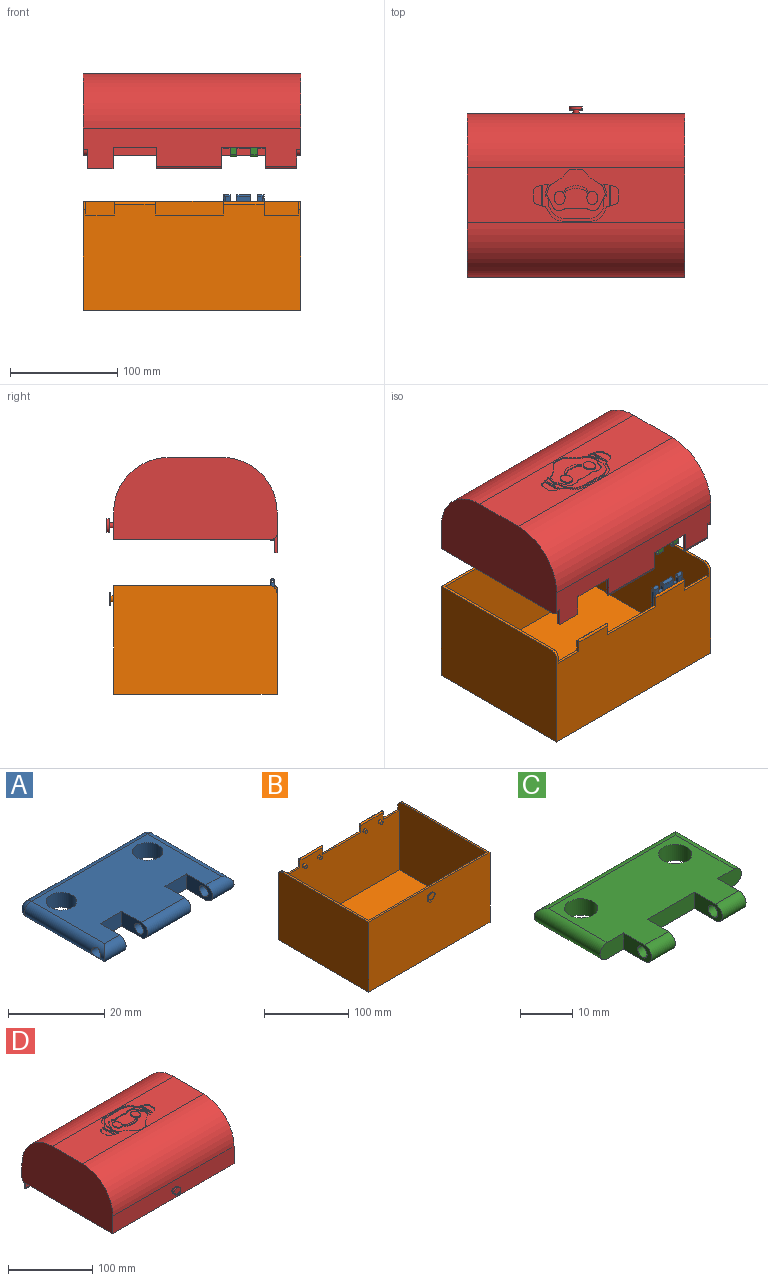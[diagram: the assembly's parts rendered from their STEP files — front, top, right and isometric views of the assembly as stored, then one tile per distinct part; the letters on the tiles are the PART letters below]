
ASSEMBLY  parts=4 mates=7
PART A: 21 faces, bbox 38.1x25.4x3.8 mm
  f0: plane 7.62x3.81mm, normal (-1,0,0), area 22.4mm2, adj f7,f8,f9,f12,f16
  f1: plane 7.62x3.81mm, normal (1,0,0), area 22.4mm2, adj f2,f8,f9,f11,f14
  f2: plane 6.35x3.81mm, normal (0,-1,0), area 24.2mm2, adj f1,f3,f8,f9
  f3: plane 7.62x3.81mm, normal (-1,0,0), area 22.4mm2, adj f2,f8,f9,f10,f13
  f4: plane 7.62x3.81mm, normal (1,0,0), area 22.4mm2, adj f7,f8,f9,f10,f13
  f5: cylinder r=3.17mm len=6.35mm, axis (0,0,-1), area 76mm2, adj f8,f9
  f6: cylinder r=3.17mm len=6.35mm, axis (0,0,-1), area 76mm2, adj f8,f9
  f7: plane 6.35x3.81mm, normal (0,-1,0), area 24.2mm2, adj f0,f4,f8,f9
  f8: plane 34.29x21.59mm, normal (0,0,1), area 604.4mm2, adj f0,f1,f2,f3,f4,f5,f6,f7
  f9: plane 34.29x21.59mm, normal (0,0,-1), area 604.4mm2, adj f0,f1,f2,f3,f4,f5,f6,f7
  f10: cylinder r=1.27mm len=12.7mm, axis (-1,0,0), area 101.3mm2, adj f3,f4
  f11: cylinder r=1.27mm len=6.35mm, axis (-1,0,0), area 48.8mm2, adj f1,f15
  f12: cylinder r=1.27mm len=6.35mm, axis (-1,0,0), area 48.8mm2, adj f0,f18
  f13: cylinder r=1.91mm len=12.7mm, axis (-1,0,0), area 76mm2, adj f3,f4,f8,f9
  f14: cylinder r=1.91mm len=6.36mm, axis (-1,0,0), area 33.9mm2, adj f1,f8,f9,f15
  f15: cylinder r=1.91mm len=23.5mm, axis (0,1,0), area 131.1mm2, adj f8,f9,f11,f14,f17
  f16: cylinder r=1.91mm len=6.36mm, axis (-1,0,0), area 33.9mm2, adj f0,f8,f9,f18
  f17: sphere r=1.91mm, area 11.4mm2, adj f15,f19
  f18: cylinder r=1.91mm len=23.5mm, axis (0,-1,0), area 131.1mm2, adj f8,f9,f12,f16,f20
  f19: cylinder r=1.91mm len=34.29mm, axis (1,0,0), area 205.2mm2, adj f8,f9,f17,f20
  f20: sphere r=1.91mm, area 11.4mm2, adj f18,f19
PART B: 39 faces, bbox 203.2x156.2x101.6 mm
  f0: plane 203.2x144.78mm, normal (0,0,1), area 1238.7mm2, adj f3,f4,f5,f7,f8,f9,f30,f31
  f1: plane 203.2x99.06mm, normal (0,1,0), area 18864.5mm2, adj f3,f5,f6,f7,f9,f19,f20,f21
  f2: plane 198.12x96.52mm, normal (0,-1,0), area 17821.8mm2, adj f7,f9,f10,f11,f13,f15,f17,f19
  f3: plane 152.4x101.6mm, normal (-1,0,0), area 15471.4mm2, adj f0,f1,f4,f6,f31
  f4: plane 203.2x101.6mm, normal (0,-1,0), area 20613.5mm2, adj f0,f3,f5,f6,f32
  f5: plane 152.4x101.6mm, normal (1,0,0), area 15471.4mm2, adj f0,f1,f4,f6,f30
  f6: plane 203.2x152.4mm, normal (0,0,-1), area 30967.7mm2, adj f1,f3,f4,f5
  f7: plane 149.86x99.06mm, normal (1,0,0), area 14613.3mm2, adj f0,f1,f2,f8,f10,f25,f31
  f8: plane 198.12x99.06mm, normal (0,1,0), area 19625.8mm2, adj f0,f7,f9,f10
  f9: plane 149.86x99.06mm, normal (-1,0,0), area 14613.3mm2, adj f0,f1,f2,f8,f10,f23,f30
  f10: plane 198.12x147.32mm, normal (0,0,1), area 29187mm2, adj f2,f7,f8,f9
  f11: cylinder r=2.22mm len=4.45mm, axis (0,1,0), area 53.2mm2, adj f2,f12
  f12: plane 4.45x4.45mm, normal (0,-1,0), area 15.5mm2, adj f11
  f13: cylinder r=2.22mm len=4.45mm, axis (0,1,0), area 53.2mm2, adj f2,f14
  f14: plane 4.45x4.45mm, normal (0,-1,0), area 15.5mm2, adj f13
  f15: cylinder r=2.22mm len=4.45mm, axis (0,1,0), area 53.2mm2, adj f2,f16
  f16: plane 4.45x4.45mm, normal (0,-1,0), area 15.5mm2, adj f15
  f17: cylinder r=2.22mm len=4.45mm, axis (0,1,0), area 53.2mm2, adj f2,f18
  f18: plane 4.45x4.45mm, normal (0,-1,0), area 15.5mm2, adj f17
  f19: plane 12.36x2.54mm, normal (1,0,0), area 29.8mm2, adj f1,f2,f21,f28,f29
  f20: plane 12.36x2.54mm, normal (-1,0,0), area 29.8mm2, adj f1,f2,f21,f26,f27
  f21: plane 63.5x2.54mm, normal (0,0,1), area 161.3mm2, adj f1,f2,f19,f20
  f22: plane 12.36x2.54mm, normal (1,0,0), area 29.8mm2, adj f1,f2,f23,f26,f27
  f23: plane 26.67x2.54mm, normal (0,0,1), area 67.7mm2, adj f1,f2,f9,f22
  f24: plane 12.36x2.54mm, normal (-1,0,0), area 29.8mm2, adj f1,f2,f25,f28,f29
  f25: plane 31.75x2.54mm, normal (0,0,1), area 80.6mm2, adj f1,f2,f7,f24
  f26: cylinder r=2.54mm len=38.1mm, axis (-1,0,0), area 101.3mm2, adj f2,f20,f22,f27
  f27: cylinder r=2.54mm len=38.1mm, axis (1,0,0), area 101.3mm2, adj f1,f20,f22,f26
  f28: cylinder r=2.54mm len=38.1mm, axis (-1,0,0), area 101.3mm2, adj f2,f19,f24,f29
  f29: cylinder r=2.54mm len=38.1mm, axis (1,0,0), area 101.3mm2, adj f1,f19,f24,f28
  f30: cylinder r=7.62mm len=7.62mm, axis (1,0,0), area 30.4mm2, adj f0,f1,f5,f9
  f31: cylinder r=7.62mm len=7.62mm, axis (1,0,0), area 30.4mm2, adj f0,f1,f3,f7
  f32: cylinder r=3.17mm len=6.35mm, axis (0,1,0), area 60.1mm2, adj f4,f35,f36,f37,f38
  f33: cylinder r=6.35mm len=12.7mm, axis (0,1,0), area 32.8mm2, adj f34,f36,f37,f38
  f34: plane 6.27x5.02mm, normal (0.78,0,0.62), area 10.2mm2, adj f33,f35,f37,f38
  f35: cylinder r=3.17mm len=2.1mm, axis (0,1,0), area 3.1mm2, adj f32,f34,f37,f38
  f36: cylinder r=3.17mm len=5.06mm, axis (0,1,0), area 8.4mm2, adj f32,f33,f37,f38
  f37: plane 12.7x12.07mm, normal (0,-1,0), area 96.2mm2, adj f32,f33,f34,f35,f36
  f38: plane 12.7x12.07mm, normal (0,1,0), area 64.5mm2, adj f32,f33,f34,f35,f36
PART C: 18 faces, bbox 38.1x25.4x3.8 mm
  f0: plane 6.35x3.81mm, normal (0,-1,0), area 22.6mm2, adj f1,f9,f10,f15
  f1: plane 7.62x3.81mm, normal (-1,0,0), area 22.4mm2, adj f0,f9,f10,f12,f14
  f2: plane 7.62x3.81mm, normal (1,0,0), area 22.4mm2, adj f3,f9,f10,f12,f14
  f3: plane 12.7x3.81mm, normal (0,-1,0), area 48.4mm2, adj f2,f4,f9,f10
  f4: plane 7.62x3.81mm, normal (-1,0,0), area 22.4mm2, adj f3,f9,f10,f11,f13
  f5: plane 7.62x3.81mm, normal (1,0,0), area 22.4mm2, adj f6,f9,f10,f11,f13
  f6: plane 6.35x3.81mm, normal (0,-1,0), area 22.6mm2, adj f5,f9,f10,f16
  f7: cylinder r=3.17mm len=6.35mm, axis (0,0,-1), area 76mm2, adj f9,f10
  f8: cylinder r=3.17mm len=6.35mm, axis (0,0,-1), area 76mm2, adj f9,f10
  f9: plane 34.29x21.59mm, normal (0,0,1), area 553.6mm2, adj f0,f1,f2,f3,f4,f5,f6,f7
  f10: plane 34.29x21.59mm, normal (0,0,-1), area 553.6mm2, adj f0,f1,f2,f3,f4,f5,f6,f7
  f11: cylinder r=1.27mm len=6.35mm, axis (-1,0,0), area 50.7mm2, adj f4,f5
  f12: cylinder r=1.27mm len=6.35mm, axis (-1,0,0), area 50.7mm2, adj f1,f2
  f13: cylinder r=1.91mm len=6.35mm, axis (-1,0,0), area 38mm2, adj f4,f5,f9,f10
  f14: cylinder r=1.91mm len=6.35mm, axis (-1,0,0), area 38mm2, adj f1,f2,f9,f10
  f15: cylinder r=1.91mm len=17.79mm, axis (0,1,0), area 102.3mm2, adj f0,f9,f10,f17
  f16: cylinder r=1.91mm len=17.79mm, axis (0,-1,0), area 102.3mm2, adj f6,f9,f10,f17
  f17: cylinder r=1.91mm len=38.11mm, axis (1,0,0), area 219.7mm2, adj f9,f10,f15,f16
PART D: 136 faces, bbox 203.2x158.8x88.9 mm
  f0: plane 203.2x147.32mm, normal (0,0,-1), area 1251.6mm2, adj f2,f3,f4,f8,f9,f10,f94,f97
  f1: plane 203.2x50.8mm, normal (0,0,1), area 8219.7mm2, adj f2,f4,f6,f7,f22,f23,f24,f25
  f2: plane 152.4x76.2mm, normal (-1,0,0), area 10499.7mm2, adj f0,f1,f3,f5,f6,f7,f97
  f3: plane 203.2x25.4mm, normal (0,-1,0), area 5141mm2, adj f0,f2,f4,f6,f15
  f4: plane 152.4x76.2mm, normal (1,0,0), area 10499.7mm2, adj f0,f1,f3,f5,f6,f7,f94
  f5: plane 203.2x38.1mm, normal (0,1,0), area 5725.8mm2, adj f2,f4,f7,f81,f82,f83,f84,f85
  f6: cylinder r=50.8mm len=203.2mm, axis (-1,0,0), area 16214.6mm2, adj f1,f2,f3,f4
  f7: cylinder r=50.8mm len=203.2mm, axis (1,0,0), area 16214.6mm2, adj f1,f2,f4,f5
  f8: plane 147.32x73.66mm, normal (1,0,0), area 9851.4mm2, adj f0,f9,f11,f12,f13,f14,f97
  f9: plane 198.12x25.4mm, normal (0,1,0), area 5032.2mm2, adj f0,f8,f10,f13
  f10: plane 147.32x73.66mm, normal (-1,0,0), area 9851.4mm2, adj f0,f9,f11,f12,f13,f14,f94
  f11: plane 198.12x38.1mm, normal (0,-1,0), area 5552.7mm2, adj f8,f10,f14,f73,f75,f77,f79,f81
  f12: plane 198.12x50.8mm, normal (0,0,-1), area 10064.5mm2, adj f8,f10,f13,f14
  f13: cylinder r=48.26mm len=198.12mm, axis (-1,0,0), area 15018.8mm2, adj f8,f9,f10,f12
  f14: cylinder r=48.26mm len=198.12mm, axis (1,0,0), area 15018.8mm2, adj f8,f10,f11,f12
  f15: cylinder r=2.54mm len=6.35mm, axis (0,1,0), area 74.4mm2, adj f3,f16,f19,f20,f21
  f16: cylinder r=3.17mm len=2.81mm, axis (0,1,0), area 8.1mm2, adj f15,f17,f20,f21
  f17: plane 6.27x5.02mm, normal (-0.78,0,0.62), area 20.4mm2, adj f16,f18,f20,f21
  f18: cylinder r=6.35mm len=12.7mm, axis (0,1,0), area 65.6mm2, adj f17,f19,f20,f21
  f19: cylinder r=3.17mm len=5.08mm, axis (0,1,0), area 18.7mm2, adj f15,f18,f20,f21
  f20: plane 12.7x12.07mm, normal (0,-1,0), area 92.1mm2, adj f15,f16,f17,f18,f19
  f21: plane 12.7x12.07mm, normal (0,1,0), area 71.9mm2, adj f15,f16,f17,f18,f19
  f22: plane 3.86x1.27mm, normal (-0.26,-0.97,0), area 5.1mm2, adj f1,f23,f26,f105
  f23: plane 19.05x1.27mm, normal (1,0,0), area 24.2mm2, adj f1,f22,f24,f26
  f24: plane 3.86x1.27mm, normal (-0.26,0.97,0), area 5.1mm2, adj f1,f23,f26,f104
  f25: plane 7.17x1.27mm, normal (-1,0,0), area 9.1mm2, adj f1,f26,f104,f105
  f26: plane 19.05x7.62mm, normal (0,0,1), area 123.8mm2, adj f22,f23,f24,f25,f104,f105
  f27: extruded ~20.32x3.44mm, area 27.9mm2, adj f43,f72,f124,f125
  f28: extruded ~18.8x2.91mm, area 25.4mm2, adj f43,f72,f124,f125
  f29: plane 1.27x0.9mm, normal (0.73,-0.69,0), area 1.6mm2, adj f1,f43,f123,f126
  f30: plane 5.63x1.67mm, normal (0.96,0.28,0), area 7.5mm2, adj f1,f43,f111,f123
  f31: plane 1.27x0.92mm, normal (0.77,0.64,0), area 1.5mm2, adj f1,f43,f96,f131
  f32: plane 7.96x1.27mm, normal (0,1,0), area 10.1mm2, adj f1,f43,f95,f96
  f33: plane 1.27x0.92mm, normal (-0.77,0.64,0), area 1.5mm2, adj f1,f43,f95,f128
  f34: plane 5.63x1.67mm, normal (-0.96,0.28,0), area 7.5mm2, adj f1,f43,f110,f122
  f35: plane 1.27x0.9mm, normal (-0.73,-0.69,0), area 1.6mm2, adj f1,f43,f122,f127
  f36: plane 8.22x3.57mm, normal (-0.92,-0.4,0), area 11.4mm2, adj f1,f43,f103,f127
  f37: plane 2.84x1.27mm, normal (0,-1,0), area 3.6mm2, adj f1,f43,f102,f103
  f38: plane 8.49x1.27mm, normal (0,-1,0), area 10.8mm2, adj f1,f43,f100,f101
  f39: plane 2.84x1.27mm, normal (0,-1,0), area 3.6mm2, adj f1,f43,f98,f99
  f40: plane 8.22x3.57mm, normal (0.92,-0.4,0), area 11.4mm2, adj f1,f43,f98,f126
  f41: extruded ~12.7x10.16mm, area 45.7mm2, adj f43,f70
  f42: extruded ~12.7x10.16mm, area 45.7mm2, adj f43,f71
  f43: plane 54.51x38.1mm, normal (0,0,1), area 1258.9mm2, adj f27,f28,f29,f30,f31,f32,f33,f34
  f44: plane 4.12x1.56mm, normal (0.94,-0.35,0), area 5.6mm2, adj f1,f64,f121,f132
  f45: plane 1.27x0.61mm, normal (0,-1,0), area 0.8mm2, adj f1,f46,f64,f121
  f46: plane 19.64x1.27mm, normal (1,0,0), area 24.9mm2, adj f1,f45,f47,f64
  f47: plane 3.47x1.27mm, normal (0.26,0.97,0), area 4.6mm2, adj f1,f46,f48,f64
  f48: plane 1.27x0.35mm, normal (0,1,0), area 0.4mm2, adj f1,f47,f64,f117
  f49: plane 9.02x2.67mm, normal (-0.96,-0.28,0), area 11.9mm2, adj f1,f64,f116,f117
  f50: plane 1.45x1.38mm, normal (-0.73,0.69,0), area 2.5mm2, adj f1,f64,f115,f116
  f51: plane 5.09x1.27mm, normal (-1,0,0), area 6.5mm2, adj f1,f64,f115,f120
  f52: plane 2.78x1.27mm, normal (-0.94,0.35,0), area 3.8mm2, adj f1,f64,f120,f135
  f53: plane 24.39x1.27mm, normal (0,1,0), area 31mm2, adj f1,f64,f134,f135
  f54: plane 5.03x3.28mm, normal (0.84,0.55,0), area 7.6mm2, adj f1,f64,f119,f134
  f55: plane 4.8x1.27mm, normal (1,0,0), area 6.1mm2, adj f1,f64,f114,f119
  f56: plane 1.45x1.38mm, normal (0.73,0.69,0), area 2.5mm2, adj f1,f64,f113,f114
  f57: plane 9.02x2.67mm, normal (0.96,-0.28,0), area 11.9mm2, adj f1,f64,f112,f113
  f58: plane 1.27x0.35mm, normal (0,1,0), area 0.4mm2, adj f1,f59,f64,f112
  f59: plane 3.47x1.27mm, normal (-0.26,0.97,0), area 4.6mm2, adj f1,f58,f60,f64
  f60: plane 19.64x1.27mm, normal (-1,0,0), area 24.9mm2, adj f1,f59,f61,f64
  f61: plane 1.27x0.67mm, normal (0,-1,0), area 0.9mm2, adj f1,f60,f64,f118
  f62: plane 7.05x4.6mm, normal (-0.84,-0.55,0), area 10.7mm2, adj f1,f64,f118,f133
  f63: plane 27.52x1.27mm, normal (0,-1,0), area 35mm2, adj f1,f64,f132,f133
  f64: plane 61.98x34.54mm, normal (0,0,1), area 343.4mm2, adj f44,f45,f46,f47,f48,f49,f50,f51
  f65: plane 19.05x1.27mm, normal (-1,0,0), area 24.2mm2, adj f1,f66,f68,f69
  f66: plane 3.86x1.27mm, normal (0.26,-0.97,0), area 5.1mm2, adj f1,f65,f69,f107
  f67: plane 7.17x1.27mm, normal (1,0,0), area 9.1mm2, adj f1,f69,f106,f107
  f68: plane 3.86x1.27mm, normal (0.26,0.97,0), area 5.1mm2, adj f1,f65,f69,f106
  f69: plane 19.05x7.62mm, normal (0,0,1), area 123.8mm2, adj f65,f66,f67,f68,f106,f107
  f70: plane 12.7x10.16mm, normal (0,0,1), area 101.3mm2, adj f41
  f71: plane 12.7x10.16mm, normal (0,0,1), area 101.3mm2, adj f42
  f72: plane 20.78x5.98mm, normal (0,0,1), area 50.4mm2, adj f27,f28,f124,f125
  f73: cylinder r=2.54mm len=5.08mm, axis (0,1,0), area 60.8mm2, adj f11,f74
  f74: plane 5.08x5.08mm, normal (0,-1,0), area 20.3mm2, adj f73
  f75: cylinder r=2.54mm len=5.08mm, axis (0,1,0), area 60.8mm2, adj f11,f76
  f76: plane 5.08x5.08mm, normal (0,-1,0), area 20.3mm2, adj f75
  f77: cylinder r=2.54mm len=5.08mm, axis (0,1,0), area 60.8mm2, adj f11,f78
  f78: plane 5.08x5.08mm, normal (0,-1,0), area 20.3mm2, adj f77
  f79: cylinder r=2.54mm len=5.08mm, axis (0,1,0), area 60.8mm2, adj f11,f80
  f80: plane 5.08x5.08mm, normal (0,-1,0), area 20.3mm2, adj f79
  f81: plane 17.44x2.54mm, normal (-1,0,0), area 34.7mm2, adj f5,f11,f90,f91,f97
  f82: plane 19.98x2.54mm, normal (1,0,0), area 49.1mm2, adj f5,f11,f90,f91,f93
  f83: plane 19.98x2.54mm, normal (-1,0,0), area 49.1mm2, adj f5,f11,f88,f89,f93
  f84: plane 19.98x2.54mm, normal (1,0,0), area 49.1mm2, adj f5,f11,f88,f89,f92
  f85: plane 20.32x2.54mm, normal (-1,0,0), area 51.6mm2, adj f5,f11,f87,f92
  f86: plane 17.78x2.54mm, normal (1,0,0), area 37.2mm2, adj f5,f11,f87,f94
  f87: plane 24.13x2.54mm, normal (0,0,-1), area 61.3mm2, adj f5,f11,f85,f86
  f88: cylinder r=2.54mm len=60.96mm, axis (-1,0,0), area 162.1mm2, adj f11,f83,f84,f89
  f89: cylinder r=2.54mm len=60.96mm, axis (1,0,0), area 162.1mm2, adj f5,f83,f84,f88
  f90: cylinder r=2.54mm len=29.21mm, axis (-1,0,0), area 77.7mm2, adj f11,f81,f82,f91
  f91: cylinder r=2.54mm len=29.21mm, axis (1,0,0), area 77.7mm2, adj f5,f81,f82,f90
  f92: plane 40.64x2.54mm, normal (0,0,-1), area 103.2mm2, adj f5,f11,f84,f85
  f93: plane 40.64x2.54mm, normal (0,0,-1), area 103.2mm2, adj f5,f11,f82,f83
  f94: cylinder r=5.08mm len=5.08mm, axis (-1,0,0), area 27mm2, adj f0,f4,f5,f10,f11,f86
  f95: cylinder r=5.08mm len=3.89mm, axis (0,0,-1), area 5.6mm2, adj f1,f32,f33,f43
  f96: cylinder r=5.08mm len=3.89mm, axis (0,0,-1), area 5.6mm2, adj f1,f31,f32,f43
  f97: cylinder r=5.08mm len=5.08mm, axis (-1,0,0), area 27mm2, adj f0,f2,f5,f8,f11,f81
  f98: cylinder r=5.08mm len=4.66mm, axis (0,0,-1), area 7.5mm2, adj f1,f39,f40,f43
  f99: cylinder r=5.08mm len=3.04mm, axis (0,0,1), area 4.1mm2, adj f1,f39,f43,f108
  f100: cylinder r=5.08mm len=1.91mm, axis (0,0,1), area 2.5mm2, adj f1,f38,f43,f108
  f101: cylinder r=5.08mm len=1.91mm, axis (0,0,1), area 2.5mm2, adj f1,f38,f43,f109
  f102: cylinder r=5.08mm len=3.04mm, axis (0,0,-1), area 4.1mm2, adj f1,f37,f43,f109
  f103: cylinder r=5.08mm len=4.66mm, axis (0,0,1), area 7.5mm2, adj f1,f36,f37,f43
  f104: cylinder r=5.08mm len=4.91mm, axis (0,0,1), area 8.4mm2, adj f1,f24,f25,f26
  f105: cylinder r=5.08mm len=4.91mm, axis (0,0,-1), area 8.4mm2, adj f1,f22,f25,f26
  f106: cylinder r=5.08mm len=4.91mm, axis (0,0,1), area 8.4mm2, adj f1,f67,f68,f69
  f107: cylinder r=5.08mm len=4.91mm, axis (0,0,-1), area 8.4mm2, adj f1,f66,f67,f69
  f108: cylinder r=5.08mm len=4.95mm, axis (0,0,1), area 6.6mm2, adj f1,f43,f99,f100
  f109: cylinder r=5.08mm len=4.95mm, axis (0,0,1), area 6.6mm2, adj f1,f43,f101,f102
  f110: cylinder r=5.08mm len=3.08mm, axis (0,0,-1), area 5.2mm2, adj f1,f34,f43,f129
  f111: cylinder r=5.08mm len=3.08mm, axis (0,0,-1), area 5.2mm2, adj f1,f30,f43,f130
  f112: cylinder r=2.54mm len=1.27mm, axis (0,0,-1), area 1.7mm2, adj f1,f57,f58,f64
  f113: cylinder r=2.54mm len=2.47mm, axis (0,0,1), area 3.4mm2, adj f1,f56,f57,f64
  f114: cylinder r=2.54mm len=1.75mm, axis (0,0,-1), area 2.4mm2, adj f1,f55,f56,f64
  f115: cylinder r=2.54mm len=1.75mm, axis (0,0,-1), area 2.4mm2, adj f1,f50,f51,f64
  f116: cylinder r=2.54mm len=2.47mm, axis (0,0,1), area 3.4mm2, adj f1,f49,f50,f64
  f117: cylinder r=2.54mm len=1.27mm, axis (0,0,1), area 1.7mm2, adj f1,f48,f49,f64
  f118: cylinder r=2.54mm len=2.13mm, axis (0,0,1), area 3.2mm2, adj f1,f61,f62,f64
  f119: cylinder r=2.54mm len=1.39mm, axis (0,0,1), area 1.9mm2, adj f1,f54,f55,f64
  f120: cylinder r=2.54mm len=1.27mm, axis (0,0,1), area 1.2mm2, adj f1,f51,f52,f64
  f121: cylinder r=2.54mm len=2.38mm, axis (0,0,1), area 3.9mm2, adj f1,f44,f45,f64
  f122: cylinder r=2.54mm len=2.47mm, axis (0,0,-1), area 3.4mm2, adj f1,f34,f35,f43
  f123: cylinder r=2.54mm len=2.47mm, axis (0,0,-1), area 3.4mm2, adj f1,f29,f30,f43
  f124: cylinder r=2.54mm len=3.07mm, axis (0,0,1), area 4.3mm2, adj f27,f28,f43,f72
  f125: cylinder r=2.54mm len=3.07mm, axis (0,0,1), area 4.3mm2, adj f27,f28,f43,f72
  f126: cylinder r=2.54mm len=1.27mm, axis (0,0,1), area 1.1mm2, adj f1,f29,f40,f43
  f127: cylinder r=2.54mm len=1.27mm, axis (0,0,1), area 1.1mm2, adj f1,f35,f36,f43
  f128: cylinder r=50.8mm len=5.45mm, axis (0,0,1), area 9.7mm2, adj f1,f33,f43,f129
  f129: cylinder r=50.8mm len=8.96mm, axis (0,0,-1), area 13.6mm2, adj f1,f43,f110,f128
  f130: cylinder r=50.8mm len=8.96mm, axis (0,0,-1), area 13.6mm2, adj f1,f43,f111,f131
  f131: cylinder r=50.8mm len=5.45mm, axis (0,0,1), area 9.7mm2, adj f1,f31,f43,f130
  f132: cylinder r=12.7mm len=11.88mm, axis (0,0,-1), area 19.5mm2, adj f1,f44,f63,f64
  f133: cylinder r=12.7mm len=10.64mm, axis (0,0,1), area 16mm2, adj f1,f62,f63,f64
  f134: cylinder r=12.7mm len=10.64mm, axis (0,0,1), area 16mm2, adj f1,f53,f54,f64
  f135: cylinder r=12.7mm len=11.88mm, axis (0,0,-1), area 19.5mm2, adj f1,f52,f53,f64
PLACE A rot(axis=(0,0.71,-0.71),180deg) t=(195.73,184.34,47.4)mm
PLACE B rot(axis=(0,0,-1),180deg) t=(230.02,330.39,-60.55)mm
PLACE C rot(axis=(1,0,0),90deg) t=(157.63,184.27,82.84)mm
PLACE D rot(axis=(0,0,1),180deg) t=(230.02,330.32,84.11)mm
MATE parallel A.f8 <-> B.f2  axis (0,-1,0) through (176.68,180.53,45.49)mm
MATE cylindrical B.f11 <-> A.f5  axis (0,1,0) through (189.38,180.53,28.35)mm
MATE parallel D.f11 <-> C.f9  axis (0,1,0) through (125.88,180.46,73.95)mm
MATE fastened C.f7 <-> D.f75  axis (0,1,0) through (163.98,182.36,101.89)mm
MATE planar C.f13 <-> A.f10  axis (-1,0,0) through (183.03,182.36,84.74)mm
MATE cylindrical C.f7 <-> D.f75  axis (0,1,0) through (163.98,182.36,101.89)mm
MATE fastened B.f11 <-> A.f5  axis (0,1,0) through (189.38,184.34,28.35)mm
